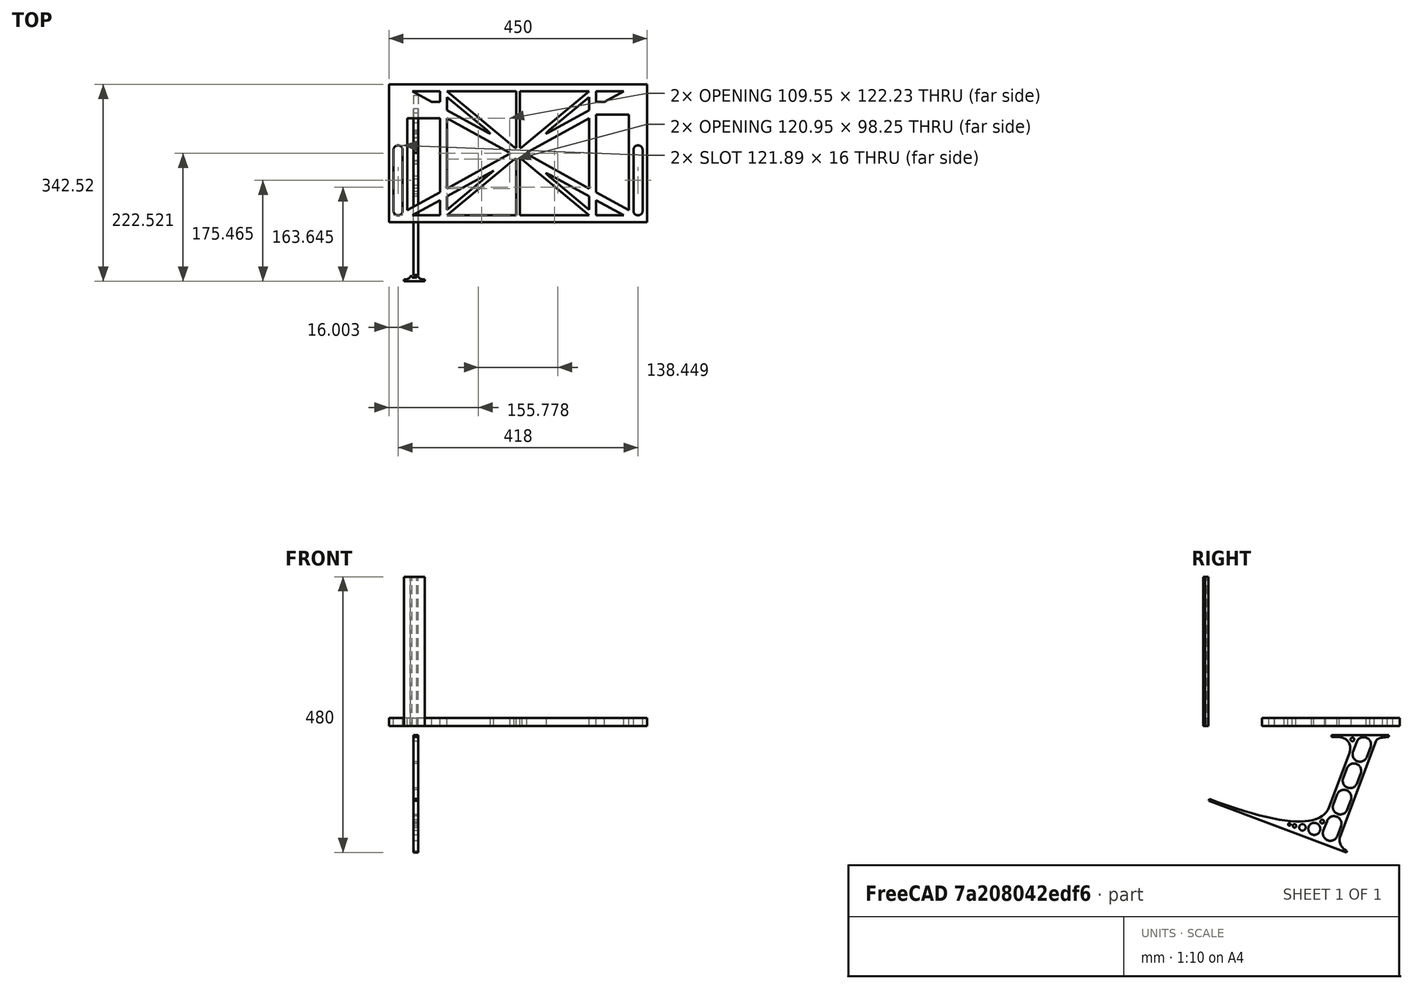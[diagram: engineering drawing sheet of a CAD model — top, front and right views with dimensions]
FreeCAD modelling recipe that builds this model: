
FCSTD DOCUMENT  (FreeCAD 0.19R0.19.2)
Label: laptopStand067
License: All rights reserved
LicenseURL: http://en.wikipedia.org/wiki/All_rights_reserved
objects: Sketcher::SketchObject×3, Part::Extrusion×3
note: 6 computed .brp shape members not serialized (recipe doc carries the construction recipe); baked Part::Feature solids carry a one-line shape summary decoded from their .brp

FEATURE [Sketcher::SketchObject] Sketch
  FullyConstrained = true
  sketch-geometry (118):
    g0: LineSegment StartX=-10.9272 StartY=-82.7794 StartZ=0 EndX=46.0728 EndY=-51.4823 EndZ=0
    g1: LineSegment StartX=366.073 StartY=-91.7794 StartZ=0 EndX=318.073 EndY=-65.424 EndZ=0
    g2: LineSegment StartX=-10.9272 StartY=77.3346 StartZ=0 EndX=-10.9272 EndY=-82.7794 EndZ=0
    g3: LineSegment StartX=375.073 StartY=-82.7794 StartZ=0 EndX=375.073 EndY=83.9235 EndZ=0
    g4: LineSegment StartX=-1.92719 StartY=-91.7794 StartZ=0 EndX=46.0728 EndY=-91.7794 EndZ=0
    g5: LineSegment StartX=318.073 StartY=124.221 StartZ=0 EndX=366.073 EndY=124.221 EndZ=0
    g6: LineSegment StartX=306.073 StartY=124.221 StartZ=0 EndX=189.124 EndY=27.0628 EndZ=0
    g7: LineSegment StartX=58.0728 StartY=-91.7794 StartZ=0 EndX=175.022 EndY=5.37834 EndZ=0
    g8: LineSegment StartX=58.0728 StartY=-81.8102 StartZ=0 EndX=58.0728 EndY=-58.8351 EndZ=0
    g9: LineSegment StartX=306.073 StartY=114.251 StartZ=0 EndX=306.073 EndY=91.2763 EndZ=0
    g10: LineSegment StartX=175.022 StartY=27.0628 StartZ=0 EndX=58.0728 EndY=124.221 EndZ=0
    g11: LineSegment StartX=139.632 StartY=-14.0532 StartZ=0 EndX=58.0728 EndY=-81.8102 EndZ=0
    g12: LineSegment StartX=139.632 StartY=-14.0532 StartZ=0 EndX=58.0728 EndY=-58.8351 EndZ=0
    g13: LineSegment StartX=189.124 StartY=5.37834 StartZ=0 EndX=306.073 EndY=-91.7794 EndZ=0
    g14: LineSegment StartX=306.073 StartY=77.3346 StartZ=0 EndX=306.073 EndY=-44.8935 EndZ=0
    g15: LineSegment StartX=318.073 StartY=83.9235 StartZ=0 EndX=318.073 EndY=-51.4823 EndZ=0
    g16: LineSegment StartX=306.073 StartY=-58.8351 StartZ=0 EndX=306.073 EndY=-81.8102 EndZ=0
    g17: LineSegment StartX=318.073 StartY=-51.4823 StartZ=0 EndX=375.073 EndY=-82.7794 EndZ=0
    g18: LineSegment StartX=318.073 StartY=-65.424 StartZ=0 EndX=318.073 EndY=-91.7794 EndZ=0
    g19: LineSegment StartX=318.073 StartY=-91.7794 StartZ=0 EndX=366.073 EndY=-91.7794 EndZ=0
    g20: LineSegment StartX=58.0728 StartY=-44.8935 StartZ=0 EndX=58.0728 EndY=77.3346 EndZ=0
    g21: LineSegment StartX=46.0728 StartY=-65.424 StartZ=0 EndX=-1.92719 EndY=-91.7794 EndZ=0
    g22: LineSegment StartX=46.0728 StartY=-65.424 StartZ=0 EndX=46.0728 EndY=-91.7794 EndZ=0
    g23: LineSegment StartX=58.0728 StartY=91.2763 StartZ=0 EndX=58.0728 EndY=114.251 EndZ=0
    g24: LineSegment StartX=46.0728 StartY=77.3346 StartZ=0 EndX=46.0728 EndY=-51.4823 EndZ=0
    g25: LineSegment StartX=-42.9272 StartY=136.221 StartZ=0 EndX=-42.9272 EndY=-103.779 EndZ=0
    g26: LineSegment StartX=407.073 StartY=136.221 StartZ=0 EndX=407.073 EndY=-103.779 EndZ=0
    g27: LineSegment StartX=179.022 StartY=27.0628 StartZ=0 EndX=179.022 EndY=124.221 EndZ=0
    g28: LineSegment StartX=185.124 StartY=27.0628 StartZ=0 EndX=185.124 EndY=124.221 EndZ=0
    g29: ArcOfCircle CenterX=-26.9272 CenterY=22.1087 CenterZ=0 NormalX=0 NormalY=0 NormalZ=1 AngleXU=0 Radius=8 StartAngle=1e-16 EndAngle=3.14159
    g30: ArcOfCircle CenterX=-26.9272 CenterY=-83.7794 CenterZ=0 NormalX=0 NormalY=0 NormalZ=1 AngleXU=0 Radius=8 StartAngle=3.14159 EndAngle=6.28319
    g31: LineSegment StartX=-34.9272 StartY=22.1087 StartZ=0 EndX=-34.9272 EndY=-83.7794 EndZ=0
    g32: LineSegment StartX=-18.9272 StartY=22.1087 StartZ=0 EndX=-18.9272 EndY=-83.7794 EndZ=0
    g33: LineSegment StartX=185.124 StartY=-91.7794 StartZ=0 EndX=306.073 EndY=-91.7794 EndZ=0
    g34: LineSegment StartX=179.022 StartY=-91.7794 StartZ=0 EndX=58.0728 EndY=-91.7794 EndZ=0
    g35: LineSegment StartX=306.073 StartY=124.221 StartZ=0 EndX=185.124 EndY=124.221 EndZ=0
    g36: LineSegment StartX=179.022 StartY=124.221 StartZ=0 EndX=58.0728 EndY=124.221 EndZ=0
    g37: ArcOfCircle CenterX=391.073 CenterY=22.1087 CenterZ=0 NormalX=0 NormalY=0 NormalZ=1 AngleXU=0 Radius=8 StartAngle=-4.4e-15 EndAngle=3.14159
    g38: LineSegment StartX=399.073 StartY=22.1087 StartZ=0 EndX=399.073 EndY=-83.7794 EndZ=0
    g39: LineSegment StartX=383.073 StartY=22.1087 StartZ=0 EndX=383.073 EndY=-83.7794 EndZ=0
    g40: ArcOfCircle CenterX=391.073 CenterY=-83.7794 CenterZ=0 NormalX=0 NormalY=0 NormalZ=1 AngleXU=0 Radius=8 StartAngle=3.14159 EndAngle=6.28319
    g41: Circle CenterX=175.022 CenterY=27.0628 CenterZ=0 NormalX=0 NormalY=0 NormalZ=1 AngleXU=0 Radius=1
    g42: Circle CenterX=179.022 CenterY=24.8665 CenterZ=0 NormalX=0 NormalY=0 NormalZ=1 AngleXU=0 Radius=1
    g43: Circle CenterX=179.022 CenterY=27.0628 CenterZ=0 NormalX=0 NormalY=0 NormalZ=1 AngleXU=0 Radius=1
    g44: BSplineCurve PolesCount=3 KnotsCount=2 Degree=2 IsPeriodic=0
    g45: GeomPoint X=175.022 Y=27.0628 Z=0
    g46: GeomPoint X=179.022 Y=27.0628 Z=0
    g47: Circle CenterX=189.124 CenterY=27.0628 CenterZ=0 NormalX=0 NormalY=0 NormalZ=1 AngleXU=0 Radius=1
    g48: Circle CenterX=185.124 CenterY=24.8665 CenterZ=0 NormalX=0 NormalY=0 NormalZ=1 AngleXU=0 Radius=1
    g49: Circle CenterX=185.124 CenterY=27.0628 CenterZ=0 NormalX=0 NormalY=0 NormalZ=1 AngleXU=0 Radius=1
    g50: BSplineCurve PolesCount=3 KnotsCount=2 Degree=2 IsPeriodic=0
    g51: GeomPoint X=189.124 Y=27.0628 Z=0
    g52: GeomPoint X=185.124 Y=27.0628 Z=0
    g53: Circle CenterX=175.022 CenterY=5.37834 CenterZ=0 NormalX=0 NormalY=0 NormalZ=1 AngleXU=0 Radius=1
    g54: Circle CenterX=179.022 CenterY=7.57463 CenterZ=0 NormalX=0 NormalY=0 NormalZ=1 AngleXU=0 Radius=1
    g55: Circle CenterX=179.022 CenterY=5.34704 CenterZ=0 NormalX=0 NormalY=0 NormalZ=1 AngleXU=0 Radius=1
    g56: BSplineCurve PolesCount=3 KnotsCount=2 Degree=2 IsPeriodic=0
    g57: GeomPoint X=175.022 Y=5.37834 Z=0
    g58: GeomPoint X=179.022 Y=5.34704 Z=0
    g59: Circle CenterX=189.124 CenterY=5.37834 CenterZ=0 NormalX=0 NormalY=0 NormalZ=1 AngleXU=0 Radius=1
    g60: Circle CenterX=185.124 CenterY=7.57463 CenterZ=0 NormalX=0 NormalY=0 NormalZ=1 AngleXU=0 Radius=1
    g61: Circle CenterX=185.124 CenterY=5.34704 CenterZ=0 NormalX=0 NormalY=0 NormalZ=1 AngleXU=0 Radius=1
    g62: BSplineCurve PolesCount=3 KnotsCount=2 Degree=2 IsPeriodic=0
    g63: GeomPoint X=189.124 Y=5.37834 Z=0
    g64: GeomPoint X=185.124 Y=5.34704 Z=0
    g65: LineSegment StartX=179.022 StartY=5.34704 StartZ=0 EndX=179.022 EndY=-91.7794 EndZ=0
    g66: LineSegment StartX=185.124 StartY=-91.7794 StartZ=0 EndX=185.124 EndY=5.34704 EndZ=0
    g67: Circle CenterX=165.871 CenterY=18.1458 CenterZ=0 NormalX=0 NormalY=0 NormalZ=1 AngleXU=0 Radius=1
    g68: Circle CenterX=169.377 CenterY=16.2206 CenterZ=0 NormalX=0 NormalY=0 NormalZ=1 AngleXU=0 Radius=1
    g69: Circle CenterX=165.871 CenterY=14.2954 CenterZ=0 NormalX=0 NormalY=0 NormalZ=1 AngleXU=0 Radius=1
    g70: BSplineCurve PolesCount=3 KnotsCount=2 Degree=2 IsPeriodic=0
    g71: GeomPoint X=165.871 Y=18.1458 Z=0
    g72: GeomPoint X=165.871 Y=14.2954 Z=0
    g73: Circle CenterX=198.275 CenterY=18.1458 CenterZ=0 NormalX=0 NormalY=0 NormalZ=1 AngleXU=0 Radius=1
    g74: Circle CenterX=194.768 CenterY=16.2206 CenterZ=0 NormalX=0 NormalY=0 NormalZ=1 AngleXU=0 Radius=1
    g75: Circle CenterX=198.275 CenterY=14.2954 CenterZ=0 NormalX=0 NormalY=0 NormalZ=1 AngleXU=0 Radius=1
    g76: BSplineCurve PolesCount=3 KnotsCount=2 Degree=2 IsPeriodic=0
    g77: GeomPoint X=198.275 Y=18.1458 Z=0
    g78: GeomPoint X=198.275 Y=14.2954 Z=0
    g79: LineSegment StartX=165.871 StartY=18.1458 StartZ=0 EndX=58.0728 EndY=77.3346 EndZ=0
    g80: LineSegment StartX=58.0728 StartY=-44.8935 StartZ=0 EndX=165.871 EndY=14.2954 EndZ=0
    g81: LineSegment StartX=198.275 StartY=18.1458 StartZ=0 EndX=306.073 EndY=77.3346 EndZ=0
    g82: LineSegment StartX=198.275 StartY=14.2954 StartZ=0 EndX=306.073 EndY=-44.8935 EndZ=0
    g83: LineSegment StartX=407.073 StartY=-103.779 StartZ=0 EndX=-42.9272 EndY=-103.779 EndZ=0
    g84: LineSegment StartX=407.073 StartY=136.221 StartZ=0 EndX=-42.9272 EndY=136.221 EndZ=0
    g85: LineSegment StartX=46.0728 StartY=77.3346 StartZ=0 EndX=-10.9272 EndY=77.3346 EndZ=0
    g86: LineSegment StartX=46.0728 StartY=105.865 StartZ=0 EndX=31.5028 EndY=105.865 EndZ=0
    g87: LineSegment StartX=46.0728 StartY=124.221 StartZ=0 EndX=46.0728 EndY=105.865 EndZ=0
    g88: LineSegment StartX=-1.92719 StartY=124.221 StartZ=0 EndX=31.5028 EndY=105.865 EndZ=0
    g89: LineSegment StartX=46.0728 StartY=124.221 StartZ=0 EndX=-1.92719 EndY=124.221 EndZ=0
    g90: LineSegment StartX=318.073 StartY=83.9235 StartZ=0 EndX=375.073 EndY=83.9235 EndZ=0
    g91: LineSegment StartX=318.073 StartY=105.865 StartZ=0 EndX=332.643 EndY=105.865 EndZ=0
    g92: LineSegment StartX=332.643 StartY=105.865 StartZ=0 EndX=366.073 EndY=124.221 EndZ=0
    g93: LineSegment StartX=318.073 StartY=124.221 StartZ=0 EndX=318.073 EndY=105.865 EndZ=0
    g94: Circle CenterX=125.607 CenterY=54.1951 CenterZ=0 NormalX=0 NormalY=0 NormalZ=1 AngleXU=0 Radius=1
    g95: Circle CenterX=139.632 CenterY=46.4944 CenterZ=0 NormalX=0 NormalY=0 NormalZ=1 AngleXU=0 Radius=1
    g96: Circle CenterX=127.325 CenterY=56.7187 CenterZ=0 NormalX=0 NormalY=0 NormalZ=1 AngleXU=0 Radius=1
    g97: BSplineCurve PolesCount=3 KnotsCount=2 Degree=2 IsPeriodic=0
    g98: GeomPoint X=125.607 Y=54.1951 Z=0
    g99: GeomPoint X=127.325 Y=56.7187 Z=0
    g100: LineSegment StartX=127.325 StartY=56.7187 StartZ=0 EndX=58.0728 EndY=114.251 EndZ=0
    g101: LineSegment StartX=58.0728 StartY=91.2763 StartZ=0 EndX=125.607 EndY=54.1951 EndZ=0
    g102: Circle CenterX=236.821 CenterY=56.7187 CenterZ=0 NormalX=0 NormalY=0 NormalZ=1 AngleXU=0 Radius=1
    g103: Circle CenterX=224.513 CenterY=46.4944 CenterZ=0 NormalX=0 NormalY=0 NormalZ=1 AngleXU=0 Radius=1
    g104: Circle CenterX=238.538 CenterY=54.1951 CenterZ=0 NormalX=0 NormalY=0 NormalZ=1 AngleXU=0 Radius=1
    g105: BSplineCurve PolesCount=3 KnotsCount=2 Degree=2 IsPeriodic=0
    g106: GeomPoint X=236.821 Y=56.7187 Z=0
    g107: GeomPoint X=238.538 Y=54.1951 Z=0
    g108: LineSegment StartX=236.821 StartY=56.7187 StartZ=0 EndX=306.073 EndY=114.251 EndZ=0
    g109: LineSegment StartX=238.538 StartY=54.1951 StartZ=0 EndX=306.073 EndY=91.2763 EndZ=0
    g110: Circle CenterX=238.538 CenterY=-21.7539 CenterZ=0 NormalX=0 NormalY=0 NormalZ=1 AngleXU=0 Radius=1
    g111: Circle CenterX=224.513 CenterY=-14.0532 CenterZ=0 NormalX=0 NormalY=0 NormalZ=1 AngleXU=0 Radius=1
    g112: Circle CenterX=236.821 CenterY=-24.2775 CenterZ=0 NormalX=0 NormalY=0 NormalZ=1 AngleXU=0 Radius=1
    g113: BSplineCurve PolesCount=3 KnotsCount=2 Degree=2 IsPeriodic=0
    g114: GeomPoint X=238.538 Y=-21.7539 Z=0
    g115: GeomPoint X=236.821 Y=-24.2775 Z=0
    g116: LineSegment StartX=238.538 StartY=-21.7539 StartZ=0 EndX=306.073 EndY=-58.8351 EndZ=0
    g117: LineSegment StartX=236.821 StartY=-24.2775 StartZ=0 EndX=306.073 EndY=-81.8102 EndZ=0
  constraints (216):
    c: Horizontal(g4)
    c: Horizontal(g5)
    c: Coincident(g12,g11)
    c: Tangent(g9,g14)
    c: Tangent(g14,g16)
    c: Coincident(g15,g17)
    c: Coincident(g18,g1)
    c: Tangent(g15,g18)
    c: Coincident(g11,g8)
    c: Tangent(g8,g20)
    c: Coincident(g12,g8)
    c: Tangent(g12,g21)
    c: Coincident(g22,g21)
    c: Coincident(g0,g24)
    c: Tangent(g20,g23)
    c: Block(g10)
    c: Block(g6)
    c: Block(g17)
    c: Block(g3)
    c: Block(g16)
    c: Block(g1)
    c: Block(g18)
    c: Block(g13)
    c: Block(g7)
    c: Block(g12)
    c: Block(g11)
    c: Block(g22)
    c: Block(g21)
    c: Block(g0)
    c: Block(g2)
    c: Block(g23)
    c: Block(g14)
    c: Block(g5)
    c: Block(g19)
    c: Block(g4)
    c: Vertical(g25)
    c: Vertical(g26)
    c: Block(g26)
    c: Block(g25)
    c: Vertical(g27)
    c: Vertical(g28)
    c: Block(g27)
    c: Block(g28)
    c: Tangent(g29,g32) = 1.5708
    c: Tangent(g29,g31) = -1.5708
    c: Tangent(g31,g30) = -1.5708
    c: Tangent(g32,g30) = 1.5708
    c: Vertical(g31)
    c: Equal(g29,g30)
    c: Block(g32)
    c: Block(g31)
    c: Coincident(g33,g13)
    c: Horizontal(g33)
    c: Coincident(g34,g7)
    c: Horizontal(g34)
    c: Coincident(g35,g6)
    c: Coincident(g35,g28)
    c: Horizontal(g35)
    c: Coincident(g36,g27)
    c: Coincident(g36,g10)
    c: Horizontal(g36)
    c: Tangent(g37,g38) = 1.5708
    c: Tangent(g38,g40) = 1.5708
    c: Equal(g37,g40)
    c: Coincident(g39,g37)
    c: Coincident(g39,g40)
    c: Block(g38)
    c: Block(g39)
    c: Coincident(g44,g10)
    c: Weight(g41) = 1
    c: Equal(g41,g42)
    c: Equal(g41,g43)
    c: Coincident(g44,g27)
    c: InternalAlignment(g41,g44)
    c: InternalAlignment(g42,g44)
    c: InternalAlignment(g43,g44)
    c: InternalAlignment(g45,g44)
    c: InternalAlignment(g46,g44)
    c: Coincident(g50,g6)
    c: Weight(g47) = 1
    c: Equal(g47,g48)
    c: Equal(g47,g49)
    c: Coincident(g50,g28)
    c: InternalAlignment(g47,g50)
    c: InternalAlignment(g48,g50)
    c: InternalAlignment(g49,g50)
    c: InternalAlignment(g51,g50)
    c: InternalAlignment(g52,g50)
    c: Block(g50)
    c: Block(g44)
    c: Coincident(g56,g7)
    c: Weight(g53) = 1
    c: Equal(g53,g54)
    c: Equal(g53,g55)
    c: InternalAlignment(g53,g56)
    c: InternalAlignment(g54,g56)
    c: InternalAlignment(g55,g56)
    c: InternalAlignment(g57,g56)
    c: InternalAlignment(g58,g56)
    c: Weight(g59) = 1
    c: Equal(g59,g60)
    c: Equal(g59,g61)
    c: InternalAlignment(g59,g62)
    c: InternalAlignment(g60,g62)
    c: InternalAlignment(g61,g62)
    c: InternalAlignment(g63,g62)
    c: InternalAlignment(g64,g62)
    c: Block(g62)
    c: Block(g56)
    c: Coincident(g65,g56)
    c: Coincident(g65,g34)
    c: Vertical(g65)
    c: Coincident(g66,g33)
    c: Coincident(g66,g62)
    c: Vertical(g66)
    c: Weight(g67) = 1
    c: Equal(g67,g68)
    c: Equal(g67,g69)
    c: InternalAlignment(g67,g70)
    c: InternalAlignment(g68,g70)
    c: InternalAlignment(g69,g70)
    c: InternalAlignment(g71,g70)
    c: InternalAlignment(g72,g70)
    c: Weight(g73) = 1
    c: Equal(g73,g74)
    c: Equal(g73,g75)
    c: InternalAlignment(g73,g76)
    c: InternalAlignment(g74,g76)
    c: InternalAlignment(g75,g76)
    c: InternalAlignment(g77,g76)
    c: InternalAlignment(g78,g76)
    c: Block(g70)
    c: Block(g76)
    c: Coincident(g79,g70)
    c: Coincident(g79,g20)
    c: Coincident(g80,g20)
    c: Coincident(g80,g70)
    c: Coincident(g81,g76)
    c: Coincident(g81,g14)
    c: Coincident(g82,g76)
    c: Coincident(g82,g14)
    c: Block(g20)
    c: Coincident(g83,g26)
    c: Coincident(g83,g25)
    c: Horizontal(g83)
    c: Distance(g83) = 450
    c: Coincident(g84,g26)
    c: Coincident(g84,g25)
    c: Horizontal(g84)
    c: Horizontal(g85)
    c: Coincident(g24,g85)
    c: Horizontal(g86)
    c: Vertical(g87)
    c: Block(g87)
    c: Block(g86)
    c: Block(g85)
    c: Distance(g87) = 18.3554
    c: Coincident(g89,g87)
    c: Coincident(g89,g88)
    c: Horizontal(g89)
    c: Block(g89)
    c: Block(g88)
    c: Coincident(g86,g88)
    c: Coincident(g2,g85)
    c: Coincident(g90,g15)
    c: Horizontal(g90)
    c: Horizontal(g91)
    c: Block(g90)
    c: Block(g9)
    c: Coincident(g92,g5)
    c: Coincident(g93,g5)
    c: Coincident(g93,g91)
    c: Vertical(g93)
    c: Block(g93)
    c: Coincident(g91,g92)
    c: Block(g92)
    c: Coincident(g3,g90)
    c: Weight(g94) = 1
    c: Equal(g94,g95)
    c: Equal(g94,g96)
    c: InternalAlignment(g94,g97)
    c: InternalAlignment(g95,g97)
    c: InternalAlignment(g96,g97)
    c: InternalAlignment(g98,g97)
    c: InternalAlignment(g99,g97)
    c: Block(g97)
    c: Coincident(g100,g97)
    c: Coincident(g100,g23)
    c: Coincident(g101,g23)
    c: Coincident(g101,g97)
    c: Weight(g102) = 1
    c: Equal(g102,g103)
    c: Equal(g102,g104)
    c: InternalAlignment(g102,g105)
    c: InternalAlignment(g103,g105)
    c: InternalAlignment(g104,g105)
    c: InternalAlignment(g106,g105)
    c: InternalAlignment(g107,g105)
    c: Block(g105)
    c: Coincident(g108,g105)
    c: Coincident(g108,g9)
    c: Coincident(g109,g105)
    c: Coincident(g109,g9)
    c: Weight(g110) = 1
    c: Equal(g110,g111)
    c: Equal(g110,g112)
    c: InternalAlignment(g110,g113)
    c: InternalAlignment(g111,g113)
    c: InternalAlignment(g112,g113)
    c: InternalAlignment(g114,g113)
    c: InternalAlignment(g115,g113)
    c: Block(g113)
    c: Coincident(g116,g113)
    c: Coincident(g116,g16)
    c: Coincident(g117,g113)
    c: Coincident(g117,g16)
FEATURE [Sketcher::SketchObject] Sketch001
  FullyConstrained = true
  MapMode = 4
  Placement = pos=(0,0,0) rot=(0.57735,0.57735,0.57735;2.0944rad)
  Support = -> [Sketch]
  sketch-geometry (46):
    g0: BSplineCurve PolesCount=3 KnotsCount=2 Degree=2 IsPeriodic=0
    g1: ArcOfCircle CenterX=73.1223 CenterY=-32.291 CenterZ=0 NormalX=0 NormalY=0 NormalZ=1 AngleXU=0 Radius=13 StartAngle=5.92268 EndAngle=9.06428
    g2: ArcOfCircle CenterX=66.7816 CenterY=-49.1439 CenterZ=0 NormalX=0 NormalY=0 NormalZ=1 AngleXU=0 Radius=13 StartAngle=2.78068 EndAngle=5.92131
    g3: ArcOfCircle CenterX=55.9263 CenterY=-78.1807 CenterZ=0 NormalX=0 NormalY=0 NormalZ=1 AngleXU=0 Radius=13 StartAngle=5.92268 EndAngle=9.06428
    g4: ArcOfCircle CenterX=49.5884 CenterY=-95.0342 CenterZ=0 NormalX=0 NormalY=0 NormalZ=1 AngleXU=0 Radius=13 StartAngle=2.78068 EndAngle=5.92131
    g5: ArcOfCircle CenterX=38.7206 CenterY=-124.067 CenterZ=0 NormalX=0 NormalY=0 NormalZ=1 AngleXU=0 Radius=13 StartAngle=5.92268 EndAngle=9.06428
    g6: ArcOfCircle CenterX=32.3875 CenterY=-140.92 CenterZ=0 NormalX=0 NormalY=0 NormalZ=1 AngleXU=0 Radius=13 StartAngle=2.78068 EndAngle=5.92131
    g7: ArcOfCircle CenterX=21.4715 CenterY=-169.934 CenterZ=0 NormalX=0 NormalY=0 NormalZ=1 AngleXU=0 Radius=13 StartAngle=5.92268 EndAngle=9.06428
    g8: ArcOfCircle CenterX=15.1336 CenterY=-186.787 CenterZ=0 NormalX=0 NormalY=0 NormalZ=1 AngleXU=0 Radius=13 StartAngle=2.78068 EndAngle=5.92131
    g9-g12: Circle x4 (B-spline internal-alignment scaffolding for g13; pole/knot coordinates omitted)
    g13: BSplineCurve PolesCount=4 KnotsCount=2 Degree=3 IsPeriodic=0
    g14: GeomPoint X=28.8094 Y=-19.0875 Z=0
    g15: GeomPoint X=47.0443 Y=-50.4712 Z=0
    g16: Circle CenterX=53.5586 CenterY=-23.2695 CenterZ=0 NormalX=0 NormalY=0 NormalZ=1 AngleXU=0 Radius=3.24518
    g17: Circle CenterX=-195.441 CenterY=-127.082 CenterZ=0 NormalX=0 NormalY=0 NormalZ=1 AngleXU=0 Radius=1
    g18: Circle CenterX=-8.24091 CenterY=-197.481 CenterZ=0 NormalX=0 NormalY=0 NormalZ=1 AngleXU=0 Radius=1
    g19: Circle CenterX=12.8789 CenterY=-141.321 CenterZ=0 NormalX=0 NormalY=0 NormalZ=1 AngleXU=0 Radius=1
    g20: BSplineCurve PolesCount=3 KnotsCount=2 Degree=2 IsPeriodic=0
    g21: GeomPoint X=-195.441 Y=-127.082 Z=0
    g22: GeomPoint X=12.8789 Y=-141.321 Z=0
    g23: Circle CenterX=-12.8016 CenterY=-179.036 CenterZ=0 NormalX=0 NormalY=0 NormalZ=1 AngleXU=0 Radius=10.5072
    g24: Circle CenterX=0.933922 CenterY=-166.43 CenterZ=0 NormalX=0 NormalY=0 NormalZ=1 AngleXU=0 Radius=3.26661
    g25: Circle CenterX=-33.5518 CenterY=-176.44 CenterZ=0 NormalX=0 NormalY=0 NormalZ=1 AngleXU=0 Radius=5.64388
    g26: Circle CenterX=-47.2366 CenterY=-173.859 CenterZ=0 NormalX=0 NormalY=0 NormalZ=1 AngleXU=0 Radius=3.01653
    g27: Circle CenterX=-56.2595 CenterY=-171.456 CenterZ=0 NormalX=0 NormalY=0 NormalZ=1 AngleXU=0 Radius=2.12826
    g28: ArcOfCircle CenterX=51.2151 CenterY=-198.473 CenterZ=0 NormalX=0 NormalY=0 NormalZ=1 AngleXU=0 Radius=20 StartAngle=2.78189 EndAngle=4.35269
    g29: LineSegment StartX=32.4951 StartY=-191.433 StartZ=0 EndX=94.6578 EndY=-26.1352 EndZ=0
    g30: LineSegment StartX=43.1192 StartY=-220.001 StartZ=0 EndX=-196.497 EndY=-129.89 EndZ=0
    g31: LineSegment StartX=43.1192 StartY=-220.001 StartZ=0 EndX=44.1752 EndY=-217.193 EndZ=0
    g32: LineSegment StartX=117.223 StartY=-19.0875 StartZ=0 EndX=117.223 EndY=-16.0875 EndZ=0
    g33: LineSegment StartX=117.223 StartY=-16.0875 StartZ=0 EndX=17.2232 EndY=-16.0875 EndZ=0
    g34: LineSegment StartX=17.2232 StartY=-16.0875 StartZ=0 EndX=17.2232 EndY=-19.0875 EndZ=0
    g35: LineSegment StartX=28.8094 StartY=-19.0875 StartZ=0 EndX=17.2232 EndY=-19.0875 EndZ=0
    g36: LineSegment StartX=47.0443 StartY=-50.4712 StartZ=0 EndX=12.8789 EndY=-141.321 EndZ=0
    g37: LineSegment StartX=-195.441 StartY=-127.082 StartZ=0 EndX=-196.497 EndY=-129.89 EndZ=0
    g38: LineSegment StartX=85.2866 StartY=-36.8766 StartZ=0 EndX=78.9396 EndY=-53.7463 EndZ=0
    g39: LineSegment StartX=60.9579 StartY=-27.7053 StartZ=0 EndX=54.6191 EndY=-44.5532 EndZ=0
    g40: LineSegment StartX=68.0907 StartY=-82.7664 StartZ=0 EndX=61.7465 EndY=-99.6365 EndZ=0
    g41: LineSegment StartX=43.7619 StartY=-73.595 StartZ=0 EndX=37.426 EndY=-90.4435 EndZ=0
    g42: LineSegment StartX=50.885 StartY=-128.652 StartZ=0 EndX=44.5456 EndY=-145.522 EndZ=0
    g43: LineSegment StartX=26.5562 StartY=-119.481 StartZ=0 EndX=20.2251 EndY=-136.329 EndZ=0
    g44: LineSegment StartX=9.3071 StartY=-165.349 StartZ=0 EndX=2.97115 EndY=-182.197 EndZ=0
    g45: LineSegment StartX=33.6358 StartY=-174.52 StartZ=0 EndX=27.2917 EndY=-191.39 EndZ=0
  constraints (71):
    c: Block(g0)
    c: Block(g1)
    c: Block(g2)
    c: Block(g4)
    c: Block(g3)
    c: Block(g6)
    c: Block(g5)
    c: Block(g8)
    c: Block(g7)
    c: Weight(g9) = 1
    c: Equal(g9,g10)
    c: Equal(g9,g11)
    c: Equal(g9,g12)
    c: InternalAlignment(g9-g12 -> g13) x4
    c: InternalAlignment(g14,g13)
    c: InternalAlignment(g15,g13)
    c: Block(g16)
    c: Weight(g17) = 1
    c: Equal(g17,g18)
    c: Equal(g17,g19)
    c: InternalAlignment(g17,g20)
    c: InternalAlignment(g18,g20)
    c: InternalAlignment(g19,g20)
    c: InternalAlignment(g21,g20)
    c: InternalAlignment(g22,g20)
    c: Block(g20)
    c: Block(g23)
    c: Block(g24)
    c: Block(g25)
    c: Block(g26)
    c: Block(g27)
    c: Block(g28)
    c: Coincident(g29,g28)
    c: Coincident(g29,g0)
    c: Block(g13)
    c: Coincident(g31,g30)
    c: Coincident(g31,g28)
    c: Block(g31)
    c: Coincident(g32,g0)
    c: Vertical(g32)
    c: Coincident(g33,g32)
    c: Horizontal(g33)
    c: Coincident(g34,g33)
    c: Vertical(g34)
    c: Block(g33)
    c: Coincident(g35,g13)
    c: Coincident(g35,g34)
    c: Horizontal(g35)
    c: Coincident(g36,g13)
    c: Coincident(g36,g20)
    c: Coincident(g37,g20)
    c: Coincident(g37,g30)
    c: Block(g30)
    c: Coincident(g38,g1)
    c: Coincident(g38,g2)
    c: Coincident(g39,g1)
    c: Coincident(g39,g2)
    c: Coincident(g40,g3)
    c: Coincident(g40,g4)
    c: Coincident(g41,g3)
    c: Coincident(g41,g4)
    c: Coincident(g42,g5)
    c: Coincident(g42,g6)
    c: Coincident(g43,g5)
    c: Coincident(g43,g6)
    c: Coincident(g44,g7)
    c: Coincident(g44,g8)
    c: Coincident(g45,g7)
    c: Coincident(g45,g8)
    c: Distance(g30) = 256
    c: Distance(g33) = 100
FEATURE [Part::Extrusion] Extrude002
  Base = -> Sketch001
  Dir = (1,0,0)
  DirMode = 2
  FaceMakerClass = Part::FaceMakerBullseye
  LengthFwd = 8
  LengthRev = 0
  Solid = true
  Symmetric = false
FEATURE [Sketcher::SketchObject] Sketch002
  FullyConstrained = true
  sketch-geometry (20):
    g0: LineSegment StartX=-2.77179 StartY=-200.304 StartZ=0 EndX=5.22821 EndY=-200.304 EndZ=0
    g1: LineSegment StartX=5.22821 StartY=-200.304 StartZ=0 EndX=5.22821 EndY=-197.304 EndZ=0
    g2: LineSegment StartX=-2.77179 StartY=-200.304 StartZ=0 EndX=-2.77179 EndY=-197.304 EndZ=0
    g3: LineSegment StartX=5.22821 StartY=-197.304 StartZ=0 EndX=8.22821 EndY=-197.304 EndZ=0
    g4: LineSegment StartX=-2.77179 StartY=-197.304 StartZ=0 EndX=-5.77179 EndY=-197.304 EndZ=0
    g5: LineSegment StartX=19.2282 StartY=-203.304 StartZ=0 EndX=19.2282 EndY=-206.304 EndZ=0
    g6: LineSegment StartX=-16.7718 StartY=-203.304 StartZ=0 EndX=-16.7718 EndY=-206.304 EndZ=0
    g7: LineSegment StartX=-16.7718 StartY=-206.304 StartZ=0 EndX=19.2282 EndY=-206.304 EndZ=0
    g8: Circle CenterX=-16.7718 CenterY=-203.304 CenterZ=0 NormalX=0 NormalY=0 NormalZ=1 AngleXU=0 Radius=1
    g9: Circle CenterX=-5.77179 CenterY=-203.304 CenterZ=0 NormalX=0 NormalY=0 NormalZ=1 AngleXU=0 Radius=1
    g10: Circle CenterX=-5.77179 CenterY=-197.304 CenterZ=0 NormalX=0 NormalY=0 NormalZ=1 AngleXU=0 Radius=1
    g11: BSplineCurve PolesCount=3 KnotsCount=2 Degree=2 IsPeriodic=0
    g12: GeomPoint X=-16.7718 Y=-203.304 Z=0
    g13: GeomPoint X=-5.77179 Y=-197.304 Z=0
    g14: Circle CenterX=19.2282 CenterY=-203.304 CenterZ=0 NormalX=0 NormalY=0 NormalZ=1 AngleXU=0 Radius=1
    g15: Circle CenterX=8.22821 CenterY=-203.304 CenterZ=0 NormalX=0 NormalY=0 NormalZ=1 AngleXU=0 Radius=1
    g16: Circle CenterX=8.22821 CenterY=-197.304 CenterZ=0 NormalX=0 NormalY=0 NormalZ=1 AngleXU=0 Radius=1
    g17: BSplineCurve PolesCount=3 KnotsCount=2 Degree=2 IsPeriodic=0
    g18: GeomPoint X=19.2282 Y=-203.304 Z=0
    g19: GeomPoint X=8.22821 Y=-197.304 Z=0
  constraints (41):
    c: Horizontal(g0)
    c: Distance(g0) = 8
    c: Coincident(g1,g0)
    c: Vertical(g1)
    c: Distance(g1) = 3
    c: Coincident(g2,g0)
    c: Vertical(g2)
    c: Distance(g2) = 3
    c: Coincident(g3,g1)
    c: Horizontal(g3)
    c: Distance(g3) = 3
    c: Coincident(g4,g2)
    c: Horizontal(g4)
    c: Distance(g4) = 3
    c: Vertical(g5)
    c: Vertical(g6)
    c: Coincident(g7,g6)
    c: Coincident(g7,g5)
    c: Weight(g8) = 1
    c: Equal(g8,g9)
    c: Equal(g8,g10)
    c: Coincident(g11,g4)
    c: InternalAlignment(g8,g11)
    c: InternalAlignment(g9,g11)
    c: InternalAlignment(g10,g11)
    c: InternalAlignment(g12,g11)
    c: InternalAlignment(g13,g11)
    c: Coincident(g17,g5)
    c: Weight(g14) = 1
    c: Equal(g14,g15)
    c: Equal(g14,g16)
    c: Coincident(g17,g3)
    c: InternalAlignment(g14,g17)
    c: InternalAlignment(g15,g17)
    c: InternalAlignment(g16,g17)
    c: InternalAlignment(g18,g17)
    c: InternalAlignment(g19,g17)
    c: Block(g7)
    c: Block(g17)
    c: Block(g11)
    c: Block(g6)
FEATURE [Part::Extrusion] Extrude003
  Base = -> Sketch002
  Dir = (0,0,1)
  DirMode = 2
  FaceMakerClass = Part::FaceMakerBullseye
  LengthFwd = 260
  LengthRev = 0
  Solid = true
  Symmetric = false
FEATURE [Part::Extrusion] Extrude
  Base = -> Sketch
  Dir = (0,0,1)
  DirMode = 2
  FaceMakerClass = Part::FaceMakerBullseye
  LengthFwd = 14
  LengthRev = 0
  Solid = true
  Symmetric = false
